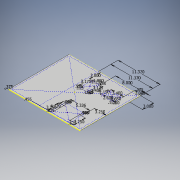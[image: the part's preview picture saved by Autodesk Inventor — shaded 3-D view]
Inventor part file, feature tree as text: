
AUTODESK INVENTOR PART (.ipt)
format: ipt  version: 2017 (Build 210142000, 142)  size: 173,056 bytes
history: native  units: in
note: dims shown in document units (in); Inventor stores cm internally (conversion verified against a paired STEP export)
features: sketch x4, hole x3, other x2, extrude x1
ambient origin geometry x8: Origin, YZ Plane, XZ Plane, XY Plane, X Axis, Y Axis, Z Axis, Center Point
bodies: Solid1 (feature_tree)
feature tree (10):
  extrude  "Extrusion1"  Depth=19.37in
  other  "bbb"
  sketch  "Sketch5"  dims[d2=0.07in d3=0.0in d4=0.375in]
  other  "bbb bob"
  hole  "wrlen holes"  [1 undecoded]
  sketch  "Sketch8"  dims[d7=5.326in d9=0.455in d10=3.25in d11=2.15in d12=3.4in d13=0.575in d14=0.575in d15=0.125in d16=0.125in d17=3.175in d18=0.25in d19=3.175in d20=1.9in d23=0.625in d24=0.625in d25=0.5in d26=0.5in d27=3.25in d28=3.25in d29=0.5in d30=0.5in d45=11.37in d46=0.134in d47=0.75in d48=0.248in d49=0.25in d50=90.0deg d51=1.0in d52=0.8108in d60=2.15in d61=3.4in d62=3.0in d63=2.0in d65=0.575in d66=0.25in d67=0.7874in d69=1.65in d70=0.7874in d72=2.6in d82=8.0in d83=3.0in d84=11.37in d85=0.1142in d86=0.75in d87=0.2165in d88=0.25in d89=90.0deg d90=1.0in d91=0.8108in d92=0.1142in d93=0.75in d94=0.2165in d95=0.25in d96=90.0deg d97=1.0in d98=0.8108in]
  hole  "bbb holes"  [1 undecoded]
  hole  "bbb bob holes"  [1 undecoded]
  sketch  "Sketch1"  dims[d0=16.45in d1=19.37in]
  sketch  "Sketch7"  dims[d5=0.375in d6=4.139in]
note: 3 required parameter values undecoded (feature->parameter linkage not recoverable at this tier; creation-order binding heuristic only, values carry confidence <= 0.55)
